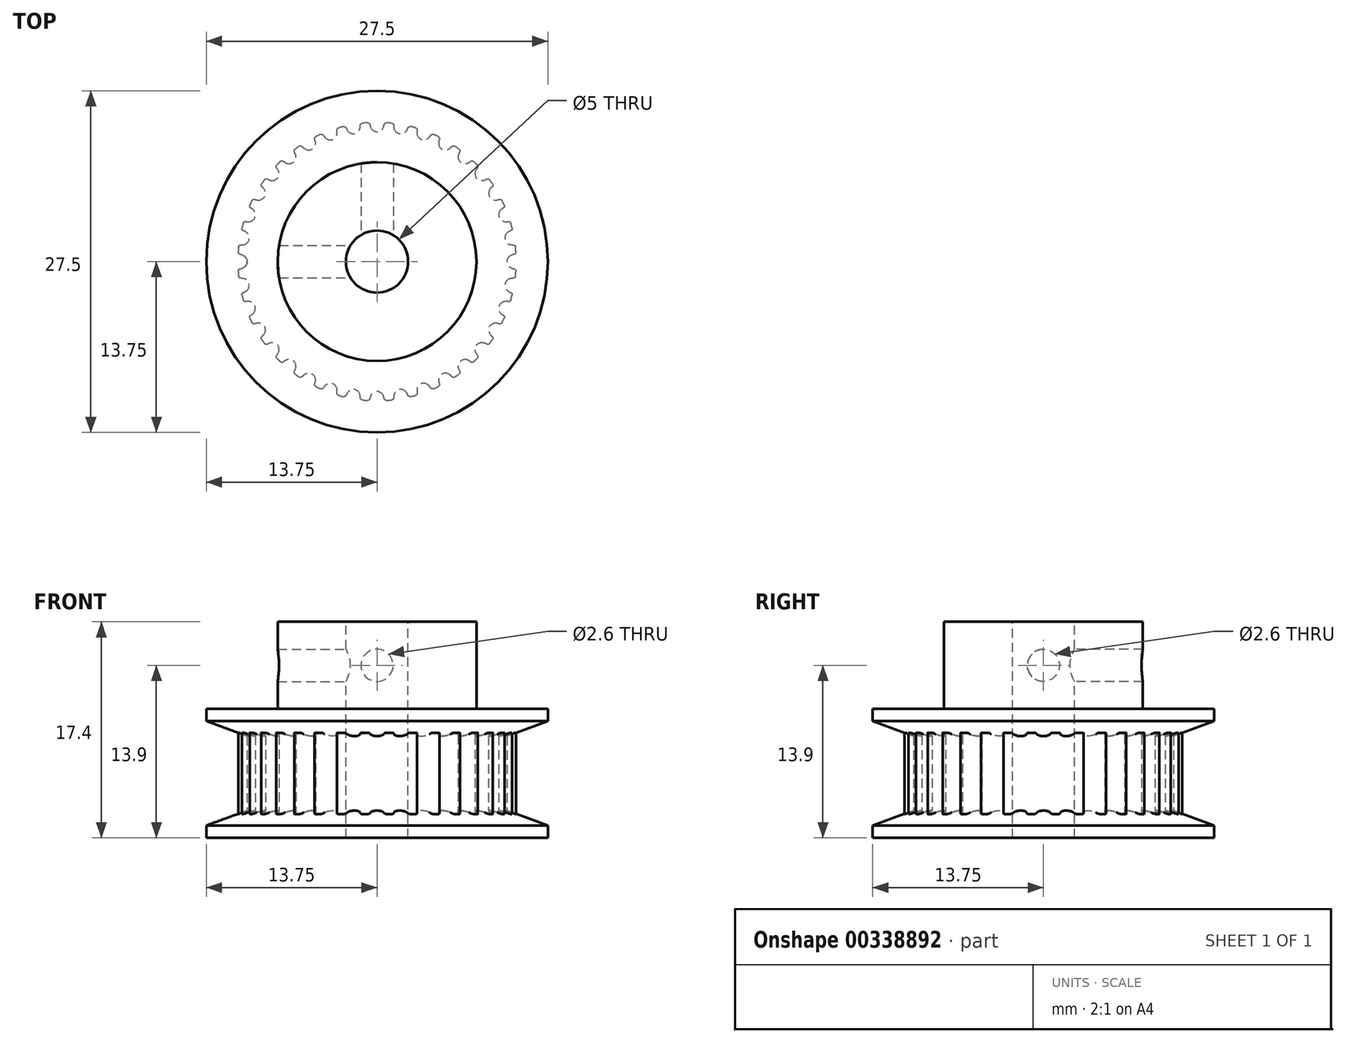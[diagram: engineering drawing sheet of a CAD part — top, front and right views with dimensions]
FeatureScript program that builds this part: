
annotation { "Feature Type Name" : "Feature", "Feature Type Description" : "" }
export const myFeature = defineFeature(function(context is Context, id is Id, definition is map)
    precondition{}
    {
        {
            assignVariable(context, id + "F0", {"name" : "teeth", "anyValue" : 36});
        }
        {
            assignVariable(context, id + "F1", {"name" : "total_length", "anyValue" : 9});
        }
        {
            var Q0;
            Q0=qCreatedBy(makeId("Top.planeOp"),FACE);
            var sketch = newSketch(context, id + "F2", { "sketchPlane" : qUnion([Q0])});
            skLineSegment(sketch, "E0", {"start": v(0, 0) * mm, "end": v(0, 10.46) * mm, "construction": true});
            skCircle(sketch, "E1", {"center": v(0, 0) * mm, "radius": 11.2 * mm});
            skPoint(sketch, "E2.MirrorCS.end.orphan", {"position": v(0.98, 11.16) * mm});
            skLineSegment(sketch, "E3", {"start": v(0.98, 11.16) * mm, "end": v(1, 11.42) * mm, "construction": true});
            skLineSegment(sketch, "E4", {"start": v(-0.98, 11.16) * mm, "end": v(-1, 11.42) * mm, "construction": true});
            skArc(sketch, "E5", {"start": v(0, 10.46) * mm, "mid": v(0.34, 10.57) * mm, "end": v(0.53, 10.86) * mm});
            skArc(sketch, "E6", {"start": v(0.53, 10.86) * mm, "mid": v(0.56, 10.96) * mm, "end": v(0.58, 11.05) * mm, "construction": true});
            skLineSegment(sketch, "E7", {"start": v(0, 10.46) * mm, "end": v(0, 11.2) * mm, "construction": true});
            skLineSegment(sketch, "E8", {"start": v(0, 11.2) * mm, "end": v(0, 11.46) * mm, "construction": true});
            skArc(sketch, "E9", {"start": v(0.58, 11.05) * mm, "mid": v(0.64, 11.15) * mm, "end": v(0.74, 11.18) * mm, "construction": true});
            skArc(sketch, "E10", {"start": v(1, 11.42) * mm, "mid": v(0, 11.46) * mm, "end": v(-1, 11.42) * mm, "construction": true});
            skLineSegment(sketch, "E11", {"start": v(0.98, 11.16) * mm, "end": v(0.91, 10.42) * mm});
            skLineSegment(sketch, "E12", {"start": v(0.91, 10.42) * mm, "end": v(0, 0) * mm});
            skLineSegment(sketch, "E13", {"start": v(0, 0) * mm, "end": v(-0.91, 10.42) * mm});
            skLineSegment(sketch, "E14", {"start": v(-0.91, 10.42) * mm, "end": v(-0.98, 11.16) * mm});
            skArc(sketch, "E15", {"start": v(0.78, 11.18) * mm, "mid": v(0.65, 11.14) * mm, "end": v(0.58, 11.04) * mm});
            skArc(sketch, "E16", {"start": v(0.53, 10.86) * mm, "mid": v(0.56, 10.95) * mm, "end": v(0.58, 11.04) * mm});
            skArc(sketch, "E17.MirrorCS", {"start": v(0, 10.46) * mm, "mid": v(-0.34, 10.57) * mm, "end": v(-0.53, 10.86) * mm});
            skArc(sketch, "E18.MirrorCS", {"start": v(-0.53, 10.86) * mm, "mid": v(-0.56, 10.95) * mm, "end": v(-0.58, 11.04) * mm});
            skArc(sketch, "E19.MirrorCS", {"start": v(-0.78, 11.18) * mm, "mid": v(-0.65, 11.14) * mm, "end": v(-0.58, 11.04) * mm});
            skArc(sketch, "E20", {"start": v(0, 11.2) * mm, "mid": v(-0.2, 11.2) * mm, "end": v(-0.4, 11.2) * mm});
            skArc(sketch, "E21", {"start": v(0.91, 10.42) * mm, "mid": v(0, 10.46) * mm, "end": v(-0.91, 10.42) * mm, "construction": true});
            skLineSegment(sketch, "E22", {"start": v(1, 11.42) * mm, "end": v(1.03, 11.8) * mm, "construction": true});
            skLineSegment(sketch, "E23", {"start": v(-1, 11.42) * mm, "end": v(-1.03, 11.8) * mm, "construction": true});
            skArc(sketch, "E24", {"start": v(-1.03, 11.8) * mm, "mid": v(0, 11.84) * mm, "end": v(1.03, 11.8) * mm, "construction": true});
            skSolve(sketch);
        }
        {
            var Q0;
            Q0=makeQuery(id+"F2.imprint","IMPRINT",FACE,{"disambiguationData":[TD([[makeQuery(id+"F2.imprint","IMPRINT",EDGE,{"derivedFrom":sQuery(id+"F2.wireOp",EDGE,"E5")}),-1.0]])]});
            var Q1;
            {var subQ1=sQuery(id+"F2.wireOp",EDGE,"E14");Q1=makeQuery(id+"F2.imprint","IMPRINT",FACE,{"disambiguationData":[TD([[makeQuery(id+"F2.imprint","IMPRINT",EDGE,{"derivedFrom":subQ1}),-1.0]])]});}
            var Q2;
            {var subQ0=sQuery(id+"F2.wireOp",EDGE,"E12");Q2=makeQuery(id+"F2.imprint","IMPRINT",FACE,{"disambiguationData":[TD([[makeQuery(id+"F2.imprint","IMPRINT",EDGE,{"derivedFrom":subQ0}),-1.0]])]});}
            extrude(context, id + "F3", {"entities" : qUnion([Q0, Q1, Q2]), "endBound" : BoundingType.SYMMETRIC, "depth" : (getVariable(context, 'total_length')) * mm});
        }
        {
            var Q0;
            Q0=makeQuery(id+"F3.opExtrude","SWEPT_BODY",BODY,{"disambiguationData":[OSD([sQuery(id+"F2.wireOp",EDGE,"E1"),sQuery(id+"F2.wireOp",EDGE,"E5"),sQuery(id+"F2.wireOp",EDGE,"E11"),sQuery(id+"F2.wireOp",EDGE,"E12"),sQuery(id+"F2.wireOp",EDGE,"E13"),sQuery(id+"F2.wireOp",EDGE,"E14"),sQuery(id+"F2.wireOp",EDGE,"E15"),sQuery(id+"F2.wireOp",EDGE,"E16"),sQuery(id+"F2.wireOp",EDGE,"E17.MirrorCS"),sQuery(id+"F2.wireOp",EDGE,"E18.MirrorCS"),sQuery(id+"F2.wireOp",EDGE,"E19.MirrorCS")])]});
            var Q1;
            Q1=makeQuery(id+"F3.opExtrude","SWEPT_EDGE",EDGE,{"disambiguationData":[OSD([sQuery(id+"F2.wireOp",EDGE,"E12"),sQuery(id+"F2.wireOp",EDGE,"E13")])]});
            circularPattern(context, id + "F4", {"operationType" : NewBodyOperationType.ADD, "entities" : qUnion([Q0]), "axis" : qUnion([Q1]), "angle" : 360 * degree, "instanceCount" : getVariable(context, 'teeth'), "equalSpace" : true});
        }
        {
            var Q0;
            Q0=qCreatedBy(makeId("Front.planeOp"),FACE);
            var sketch = newSketch(context, id + "F5", { "sketchPlane" : qUnion([Q0])});
            skLineSegment(sketch, "E25", {"start": v(0, 4.5) * mm, "end": v(13.75, 4.5) * mm});
            skLineSegment(sketch, "E26", {"start": v(13.75, 4.5) * mm, "end": v(13.75, 3.5) * mm});
            skLineSegment(sketch, "E27", {"start": v(13.75, 3.5) * mm, "end": v(10.46, 2.3) * mm});
            skLineSegment(sketch, "E28", {"start": v(10.46, 2.3) * mm, "end": v(0, 2.3) * mm});
            skLineSegment(sketch, "E29", {"start": v(0, 2.3) * mm, "end": v(0, 4.5) * mm});
            skLineSegment(sketch, "E30", {"start": v(0, -3.7) * mm, "end": v(10.46, -3.7) * mm});
            skLineSegment(sketch, "E31", {"start": v(10.46, -3.7) * mm, "end": v(13.75, -4.9) * mm});
            skLineSegment(sketch, "E32", {"start": v(13.75, -4.9) * mm, "end": v(13.75, -5.9) * mm});
            skLineSegment(sketch, "E33", {"start": v(13.75, -5.9) * mm, "end": v(0, -5.9) * mm});
            skLineSegment(sketch, "E34", {"start": v(0, -5.9) * mm, "end": v(0, -3.7) * mm});
            skSolve(sketch);
        }
        {
            var Q0;
            Q0=qSketchRegion(id+"F5",true);
            var Q1;
            Q1=sQuery(id+"F5.wireOp",EDGE,"E29");
            revolve(context, id + "F6", {"operationType" : NewBodyOperationType.ADD, "entities" : qUnion([Q0]), "axis" : qUnion([Q1]), "revolveType" : RevolveType.FULL});
        }
        {
            var Q0;
            {var subQ0=makeQuery(id+"F3.opExtrude","CAP_FACE",FACE,{"disambiguationData":[OSD([sQuery(id+"F2.wireOp",EDGE,"E1"),sQuery(id+"F2.wireOp",EDGE,"E5"),sQuery(id+"F2.wireOp",EDGE,"E11"),sQuery(id+"F2.wireOp",EDGE,"E12"),sQuery(id+"F2.wireOp",EDGE,"E13"),sQuery(id+"F2.wireOp",EDGE,"E14"),sQuery(id+"F2.wireOp",EDGE,"E15"),sQuery(id+"F2.wireOp",EDGE,"E16"),sQuery(id+"F2.wireOp",EDGE,"E17.MirrorCS"),sQuery(id+"F2.wireOp",EDGE,"E18.MirrorCS"),sQuery(id+"F2.wireOp",EDGE,"E19.MirrorCS")])],"isStart":false});Q0=makeQuery(id+"F6.boolean.opBoolean","MERGE",FACE,{"derivedFrom":[makeQuery(id+"F4.boolean.opBoolean","MERGE",FACE,{"derivedFrom":[subQ0,makeQuery(id+"F4.opPattern","COPY",FACE,{"derivedFrom":subQ0,"instanceName":"1"}),makeQuery(id+"F4.opPattern","COPY",FACE,{"derivedFrom":subQ0,"instanceName":"2"}),makeQuery(id+"F4.opPattern","COPY",FACE,{"derivedFrom":subQ0,"instanceName":"3"}),makeQuery(id+"F4.opPattern","COPY",FACE,{"derivedFrom":subQ0,"instanceName":"4"}),makeQuery(id+"F4.opPattern","COPY",FACE,{"derivedFrom":subQ0,"instanceName":"5"}),makeQuery(id+"F4.opPattern","COPY",FACE,{"derivedFrom":subQ0,"instanceName":"6"}),makeQuery(id+"F4.opPattern","COPY",FACE,{"derivedFrom":subQ0,"instanceName":"7"}),makeQuery(id+"F4.opPattern","COPY",FACE,{"derivedFrom":subQ0,"instanceName":"8"}),makeQuery(id+"F4.opPattern","COPY",FACE,{"derivedFrom":subQ0,"instanceName":"9"}),makeQuery(id+"F4.opPattern","COPY",FACE,{"derivedFrom":subQ0,"instanceName":"10"}),makeQuery(id+"F4.opPattern","COPY",FACE,{"derivedFrom":subQ0,"instanceName":"11"}),makeQuery(id+"F4.opPattern","COPY",FACE,{"derivedFrom":subQ0,"instanceName":"12"}),makeQuery(id+"F4.opPattern","COPY",FACE,{"derivedFrom":subQ0,"instanceName":"13"}),makeQuery(id+"F4.opPattern","COPY",FACE,{"derivedFrom":subQ0,"instanceName":"14"}),makeQuery(id+"F4.opPattern","COPY",FACE,{"derivedFrom":subQ0,"instanceName":"15"}),makeQuery(id+"F4.opPattern","COPY",FACE,{"derivedFrom":subQ0,"instanceName":"16"}),makeQuery(id+"F4.opPattern","COPY",FACE,{"derivedFrom":subQ0,"instanceName":"17"}),makeQuery(id+"F4.opPattern","COPY",FACE,{"derivedFrom":subQ0,"instanceName":"18"}),makeQuery(id+"F4.opPattern","COPY",FACE,{"derivedFrom":subQ0,"instanceName":"19"}),makeQuery(id+"F4.opPattern","COPY",FACE,{"derivedFrom":subQ0,"instanceName":"20"}),makeQuery(id+"F4.opPattern","COPY",FACE,{"derivedFrom":subQ0,"instanceName":"21"}),makeQuery(id+"F4.opPattern","COPY",FACE,{"derivedFrom":subQ0,"instanceName":"22"}),makeQuery(id+"F4.opPattern","COPY",FACE,{"derivedFrom":subQ0,"instanceName":"23"}),makeQuery(id+"F4.opPattern","COPY",FACE,{"derivedFrom":subQ0,"instanceName":"24"}),makeQuery(id+"F4.opPattern","COPY",FACE,{"derivedFrom":subQ0,"instanceName":"25"}),makeQuery(id+"F4.opPattern","COPY",FACE,{"derivedFrom":subQ0,"instanceName":"26"}),makeQuery(id+"F4.opPattern","COPY",FACE,{"derivedFrom":subQ0,"instanceName":"27"}),makeQuery(id+"F4.opPattern","COPY",FACE,{"derivedFrom":subQ0,"instanceName":"28"}),makeQuery(id+"F4.opPattern","COPY",FACE,{"derivedFrom":subQ0,"instanceName":"29"}),makeQuery(id+"F4.opPattern","COPY",FACE,{"derivedFrom":subQ0,"instanceName":"30"}),makeQuery(id+"F4.opPattern","COPY",FACE,{"derivedFrom":subQ0,"instanceName":"31"}),makeQuery(id+"F4.opPattern","COPY",FACE,{"derivedFrom":subQ0,"instanceName":"32"}),makeQuery(id+"F4.opPattern","COPY",FACE,{"derivedFrom":subQ0,"instanceName":"33"}),makeQuery(id+"F4.opPattern","COPY",FACE,{"derivedFrom":subQ0,"instanceName":"34"}),makeQuery(id+"F4.opPattern","COPY",FACE,{"derivedFrom":subQ0,"instanceName":"35"})]}),makeQuery(id+"F6.opRevolve","SWEPT_FACE",FACE,{"disambiguationData":[OSD([sQuery(id+"F5.wireOp",EDGE,"E25")])]})]});}
            var sketch = newSketch(context, id + "F7", { "sketchPlane" : qUnion([Q0])});
            skCircle(sketch, "E35", {"center": v(0, 0) * mm, "radius": 8 * mm});
            skSolve(sketch);
        }
        {
            var Q0;
            Q0 = qSketchRegion(id + "F7", true);
            extrude(context, id + "F8", {"entities" : qUnion([Q0]), "operationType" : NewBodyOperationType.ADD, "depth" : 7 * mm});
        }
        {
            var Q0;
            Q0=qCreatedBy(makeId("Top.planeOp"),FACE);
            var sketch = newSketch(context, id + "F9", { "sketchPlane" : qUnion([Q0])});
            skCircle(sketch, "E36", {"center": v(0, 0) * mm, "radius": 2.5 * mm});
            skSolve(sketch);
        }
        {
            var Q0;
            Q0=qSketchRegion(id+"F9",true);
            extrude(context, id + "F10", {"entities" : qUnion([Q0]), "operationType" : NewBodyOperationType.REMOVE, "endBound" : BoundingType.SYMMETRIC, "oppositeDirection" : true, "depth" : 100 * mm});
        }
        {
            var Q0;
            Q0=qCreatedBy(makeId("Front.planeOp"),FACE);
            var sketch = newSketch(context, id + "F11", { "sketchPlane" : qUnion([Q0])});
            skCircle(sketch, "E37", {"center": v(0, 8) * mm, "radius": 1.3 * mm});
            skSolve(sketch);
        }
        {
            var Q0;
            Q0 = qSketchRegion(id + "F11", true);
            extrude(context, id + "F12", {"entities" : qUnion([Q0]), "operationType" : NewBodyOperationType.REMOVE, "endBound" : BoundingType.THROUGH_ALL, "oppositeDirection" : true, "depth" : 25 * mm});
        }
        {
            var Q0;
            Q0=qCreatedBy(makeId("Right.planeOp"),FACE);
            var sketch = newSketch(context, id + "F13", { "sketchPlane" : qUnion([Q0])});
            skCircle(sketch, "E38", {"center": v(0, 8) * mm, "radius": 1.3 * mm});
            skSolve(sketch);
        }
        {
            var Q0;
            Q0 = qSketchRegion(id + "F13", true);
            extrude(context, id + "F14", {"entities" : qUnion([Q0]), "operationType" : NewBodyOperationType.REMOVE, "endBound" : BoundingType.THROUGH_ALL, "oppositeDirection" : true, "depth" : 25 * mm});
        }
    });
